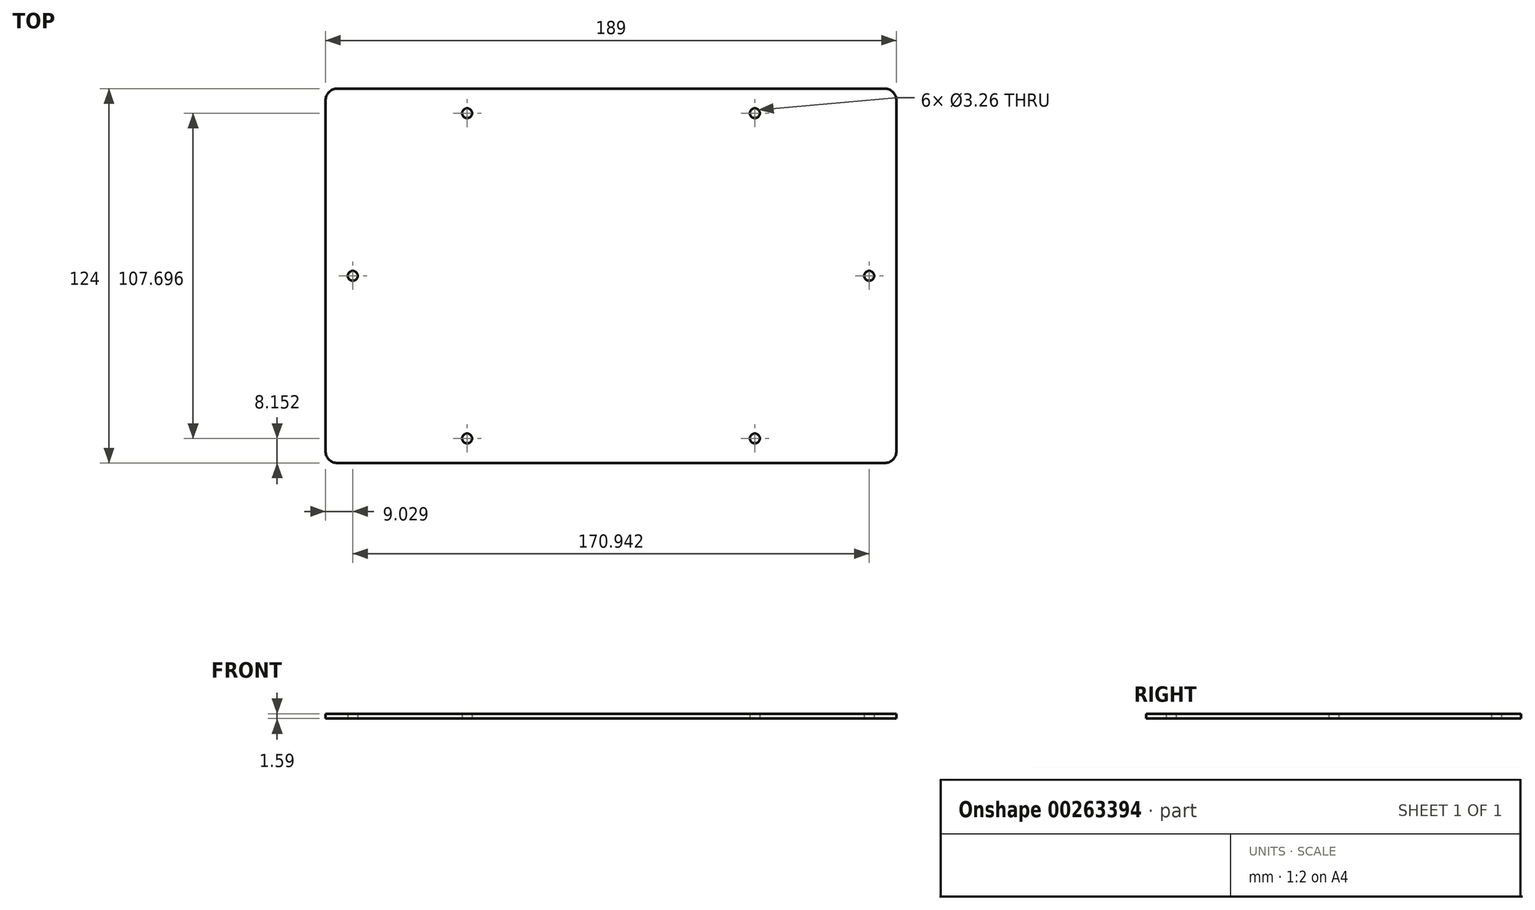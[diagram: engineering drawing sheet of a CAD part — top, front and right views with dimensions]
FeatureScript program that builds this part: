
annotation { "Feature Type Name" : "Feature", "Feature Type Description" : "" }
export const myFeature = defineFeature(function(context is Context, id is Id, definition is map)
    precondition{}
    {
        {
            var Q0;
            Q0=qCreatedBy(makeId("Top.planeOp"),FACE);
            var sketch = newSketch(context, id + "F0", { "sketchPlane" : qUnion([Q0])});
            skLineSegment(sketch, "E0.bottom", {"start": v(94.5, -62) * mm, "end": v(-94.5, -62) * mm});
            skLineSegment(sketch, "E0.top", {"start": v(94.5, 62) * mm, "end": v(-94.5, 62) * mm});
            skLineSegment(sketch, "E0.left", {"start": v(94.5, -62) * mm, "end": v(94.5, 62) * mm});
            skLineSegment(sketch, "E0.right", {"start": v(-94.5, -62) * mm, "end": v(-94.5, 62) * mm});
            skPoint(sketch, "E0.middle", {"position": v(0, 0) * mm});
            skLineSegment(sketch, "E1.bottom", {"start": v(85.47, -53.85) * mm, "end": v(-85.47, -53.85) * mm, "construction": true});
            skLineSegment(sketch, "E1.top", {"start": v(85.47, 53.85) * mm, "end": v(-85.47, 53.85) * mm, "construction": true});
            skLineSegment(sketch, "E1.left", {"start": v(85.47, -53.85) * mm, "end": v(85.47, 53.85) * mm, "construction": true});
            skLineSegment(sketch, "E1.right", {"start": v(-85.47, -53.85) * mm, "end": v(-85.47, 53.85) * mm, "construction": true});
            skCircle(sketch, "E2", {"center": v(-85.47, 0) * mm, "radius": 1.63 * mm});
            skCircle(sketch, "E3", {"center": v(-47.63, 53.85) * mm, "radius": 1.63 * mm});
            skCircle(sketch, "E4", {"center": v(-47.62, -53.85) * mm, "radius": 1.63 * mm});
            skLineSegment(sketch, "E5", {"start": v(-47.63, 53.85) * mm, "end": v(-47.62, -53.85) * mm, "construction": true});
            skCircle(sketch, "E6.MirrorC", {"center": v(47.63, 53.85) * mm, "radius": 1.63 * mm});
            skCircle(sketch, "E7.MirrorC", {"center": v(85.47, 0) * mm, "radius": 1.63 * mm});
            skCircle(sketch, "E8.MirrorC", {"center": v(47.62, -53.85) * mm, "radius": 1.63 * mm});
            skSolve(sketch);
        }
        {
            var Q0;
            Q0 = qSketchRegion(id + "F0", true);
            extrude(context, id + "F1", {"entities" : qUnion([Q0]), "depth" : 1.59 * mm});
        }
        {
            var Q0;
            Q0=makeQuery(id+"F1.opExtrude","SWEPT_EDGE",EDGE,{"disambiguationData":[OSD([sQuery(id+"F0.wireOp",EDGE,"E0.top"),sQuery(id+"F0.wireOp",EDGE,"E0.right")])]});
            var Q1;
            Q1=makeQuery(id+"F1.opExtrude","SWEPT_EDGE",EDGE,{"disambiguationData":[OSD([sQuery(id+"F0.wireOp",EDGE,"E0.bottom"),sQuery(id+"F0.wireOp",EDGE,"E0.right")])]});
            var Q2;
            Q2=makeQuery(id+"F1.opExtrude","SWEPT_EDGE",EDGE,{"disambiguationData":[OSD([sQuery(id+"F0.wireOp",EDGE,"E0.top"),sQuery(id+"F0.wireOp",EDGE,"E0.left")])]});
            var Q3;
            Q3=makeQuery(id+"F1.opExtrude","SWEPT_EDGE",EDGE,{"disambiguationData":[OSD([sQuery(id+"F0.wireOp",EDGE,"E0.bottom"),sQuery(id+"F0.wireOp",EDGE,"E0.left")])]});
            fillet(context, id + "F2", {"entities" : qUnion([Q0, Q1, Q2, Q3]), "radius" : 4 * mm, "tangentPropagation" : true, "allowEdgeOverflow" : false});
        }
    });
